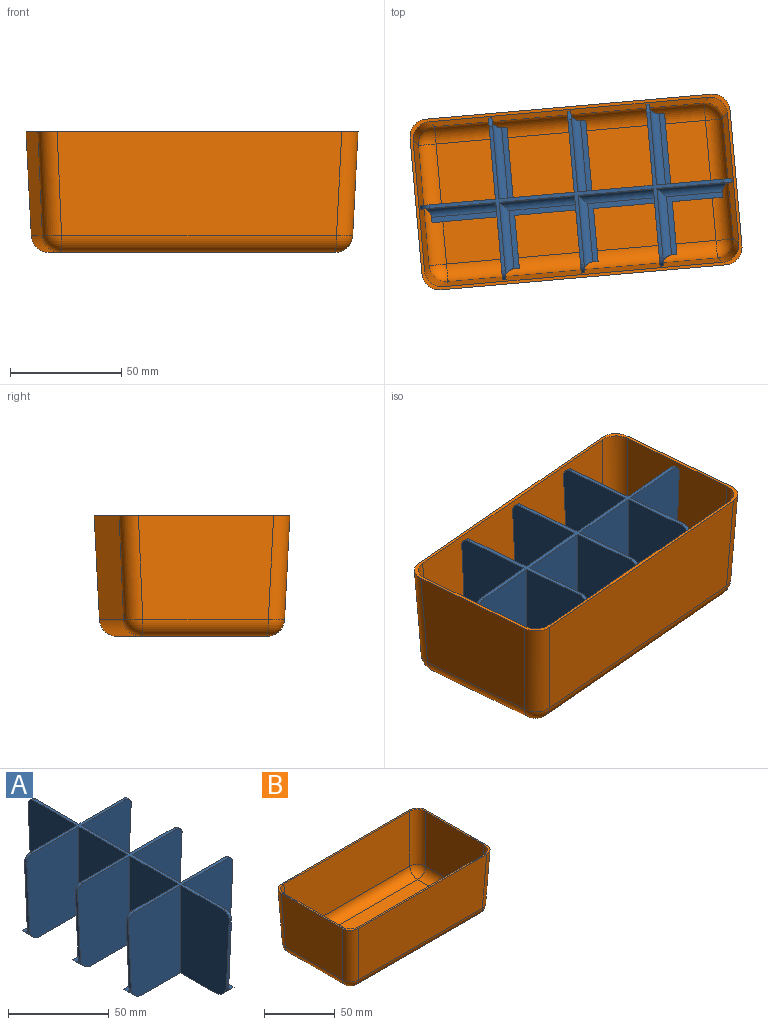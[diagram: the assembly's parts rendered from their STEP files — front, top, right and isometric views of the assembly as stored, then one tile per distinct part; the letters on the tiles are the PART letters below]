
ASSEMBLY  parts=2 mates=1
PART A: 73 faces, bbox 73.1x140.8x53 mm
  f0: plane 27.6x2mm, normal (1,0,0), area 55.2mm2, adj f8,f15,f36,f43
  f1: plane 29.36x2mm, normal (1,0,0), area 55.4mm2, adj f2,f15,f45,f54
  f2: plane 29.36x2.4mm, normal (0,0,1), area 70.5mm2, adj f1,f45,f54,f55
  f3: plane 47x34mm, normal (1,0,0), area 1598mm2, adj f17,f36,f44,f60
  f4: plane 47x34.01mm, normal (1,0,0), area 1551.4mm2, adj f17,f18,f45,f54,f55,f72
  f5: plane 53x34mm, normal (-1,0,0), area 1785.8mm2, adj f15,f17,f33,f39,f40,f41,f62
  f6: plane 53x34.01mm, normal (-1,0,0), area 1730.2mm2, adj f15,f17,f18,f42,f54,f72
  f7: plane 27.6x2mm, normal (1,0,0), area 55.2mm2, adj f12,f15,f27,f34
  f8: plane 30x26.31mm, normal (0,0,1), area 129.4mm2, adj f0,f36,f43,f48,f60,f61
  f9: plane 47x34mm, normal (1,0,0), area 1598mm2, adj f17,f27,f35,f58
  f10: plane 53x34mm, normal (-1,0,0), area 1785.8mm2, adj f15,f17,f24,f30,f31,f32,f63
  f11: plane 22.96x2mm, normal (1,0,0), area 42.6mm2, adj f15,f16,f25,f53
  f12: plane 30x26.31mm, normal (0,0,1), area 129.4mm2, adj f7,f27,f34,f50,f58,f59
  f13: plane 47x34.01mm, normal (1,0,0), area 1551.4mm2, adj f17,f19,f26,f53,f56,f71
  f14: plane 53x34.01mm, normal (-1,0,0), area 1714mm2, adj f15,f17,f19,f21,f22,f23,f53,f64
  f15: plane 120.94x53.24mm, normal (0,0,-1), area 2053.2mm2, adj f0,f1,f5,f6,f7,f10,f11,f14
  f16: plane 26.31x25.36mm, normal (0,0,1), area 118.3mm2, adj f11,f25,f52,f53,f56,f57
  f17: plane 132.81x65.11mm, normal (0,0,1), area 517.4mm2, adj f3,f4,f5,f6,f9,f10,f13,f14
  f18: plane 41.19x1.94mm, normal (0,-1,-0.05), area 66mm2, adj f4,f6,f54,f72
  f19: plane 41.19x1.94mm, normal (0,1,-0.05), area 66mm2, adj f13,f14,f53,f71
  f20: plane 41.19x1.94mm, normal (-1,0,-0.05), area 66mm2, adj f21,f24,f51,f69
  f21: plane 47x36.56mm, normal (0,1,0), area 1671.2mm2, adj f14,f17,f20,f51,f64,f69
  f22: plane 31.91x2.4mm, normal (0,0,1), area 76.6mm2, adj f14,f23,f51,f64
  f23: plane 31.91x2mm, normal (0,1,0), area 60.5mm2, adj f14,f15,f22,f51
  f24: plane 53x36.56mm, normal (0,-1,0), area 1865.4mm2, adj f10,f15,f17,f20,f51,f69
  f25: plane 23.91x2mm, normal (0,1,0), area 44.5mm2, adj f11,f15,f16,f52
  f26: plane 47x34.96mm, normal (0,1,0), area 1596mm2, adj f13,f17,f28,f52,f57,f70
  f27: plane 53x34.96mm, normal (0,-1,0), area 1764.4mm2, adj f7,f9,f12,f15,f17,f28,f52,f58
  f28: plane 41.19x1.94mm, normal (1,0,-0.05), area 66mm2, adj f26,f27,f52,f70
  f29: plane 41.19x1.94mm, normal (-1,0,-0.05), area 66mm2, adj f30,f33,f49,f67
  f30: plane 47x36.56mm, normal (0,1,0), area 1671.2mm2, adj f10,f17,f29,f49,f63,f67
  f31: plane 31.91x2.4mm, normal (0,0,1), area 76.6mm2, adj f10,f32,f49,f63
  f32: plane 31.91x2mm, normal (0,1,0), area 60.5mm2, adj f10,f15,f31,f49
  f33: plane 53x36.56mm, normal (0,-1,0), area 1865.4mm2, adj f5,f15,f17,f29,f49,f67
  f34: plane 23.91x2mm, normal (0,1,0), area 44.5mm2, adj f7,f12,f15,f50
  f35: plane 47x34.96mm, normal (0,1,0), area 1596mm2, adj f9,f17,f37,f50,f59,f68
  f36: plane 53x34.96mm, normal (0,-1,0), area 1764.4mm2, adj f0,f3,f8,f15,f17,f37,f50,f60
  f37: plane 41.19x1.94mm, normal (1,0,-0.05), area 66mm2, adj f35,f36,f50,f68
  f38: plane 41.19x1.94mm, normal (-1,0,-0.05), area 66mm2, adj f39,f42,f47,f65
  f39: plane 47x36.56mm, normal (0,1,0), area 1671.2mm2, adj f5,f17,f38,f47,f62,f65
  f40: plane 31.91x2.4mm, normal (0,0,1), area 76.6mm2, adj f5,f41,f47,f62
  f41: plane 31.91x2mm, normal (0,1,0), area 60.5mm2, adj f5,f15,f40,f47
  f42: plane 53x36.56mm, normal (0,-1,0), area 1865.4mm2, adj f6,f15,f17,f38,f47,f65
  f43: plane 23.91x2mm, normal (0,1,0), area 44.5mm2, adj f0,f8,f15,f48
  f44: plane 47x34.96mm, normal (0,1,0), area 1596mm2, adj f3,f17,f46,f48,f61,f66
  f45: plane 53x34.96mm, normal (0,-1,0), area 1764.4mm2, adj f1,f2,f4,f15,f17,f46,f48,f55
  f46: plane 41.19x1.94mm, normal (1,0,-0.05), area 66mm2, adj f44,f45,f48,f66
  f47: cylinder r=8mm len=8mm, axis (0,1,0), area 61.1mm2, adj f15,f38,f39,f40,f41,f42,f62
  f48: cylinder r=8mm len=8mm, axis (0,1,0), area 61.1mm2, adj f8,f15,f43,f44,f45,f46,f61
  f49: cylinder r=8mm len=8mm, axis (0,1,0), area 61.1mm2, adj f15,f29,f30,f31,f32,f33,f63
  f50: cylinder r=8mm len=8mm, axis (0,1,0), area 61.1mm2, adj f12,f15,f34,f35,f36,f37,f59
  f51: cylinder r=8mm len=8mm, axis (0,1,0), area 61.1mm2, adj f15,f20,f21,f22,f23,f24,f64
  f52: cylinder r=8mm len=8mm, axis (0,1,0), area 61.1mm2, adj f15,f16,f25,f26,f27,f28,f57
  f53: cylinder r=8mm len=8mm, axis (1,0,0), area 61.1mm2, adj f11,f13,f14,f15,f16,f19,f56
  f54: cylinder r=8mm len=8mm, axis (1,0,0), area 61.1mm2, adj f1,f2,f4,f6,f15,f18,f55
  f55: cylinder r=4mm len=31.82mm, axis (0,1,0), area 191.5mm2, adj f2,f4,f45,f54
  f56: cylinder r=4mm len=31.82mm, axis (0,1,0), area 182.4mm2, adj f13,f16,f53,f57
  f57: cylinder r=4mm len=32.77mm, axis (-1,0,0), area 188.4mm2, adj f16,f26,f52,f56
  f58: cylinder r=4mm len=34mm, axis (0,1,0), area 204.5mm2, adj f9,f12,f27,f59
  f59: cylinder r=4mm len=32.77mm, axis (-1,0,0), area 188.4mm2, adj f12,f35,f50,f58
  f60: cylinder r=4mm len=34mm, axis (0,1,0), area 204.5mm2, adj f3,f8,f36,f61
  f61: cylinder r=4mm len=32.77mm, axis (-1,0,0), area 188.4mm2, adj f8,f44,f48,f60
  f62: cylinder r=4mm len=34.37mm, axis (-1,0,0), area 207.6mm2, adj f5,f39,f40,f47
  f63: cylinder r=4mm len=34.37mm, axis (-1,0,0), area 207.6mm2, adj f10,f30,f31,f49
  f64: cylinder r=4mm len=34.37mm, axis (-1,0,0), area 207.6mm2, adj f14,f21,f22,f51
  f65: cylinder r=4mm len=4.19mm, axis (0,-1,0), area 10.4mm2, adj f17,f38,f39,f42
  f66: cylinder r=4mm len=4.19mm, axis (0,-1,0), area 10.4mm2, adj f17,f44,f45,f46
  f67: cylinder r=4mm len=4.19mm, axis (0,-1,0), area 10.4mm2, adj f17,f29,f30,f33
  f68: cylinder r=4mm len=4.19mm, axis (0,-1,0), area 10.4mm2, adj f17,f35,f36,f37
  f69: cylinder r=4mm len=4.19mm, axis (0,-1,0), area 10.4mm2, adj f17,f20,f21,f24
  f70: cylinder r=4mm len=4.19mm, axis (0,-1,0), area 10.4mm2, adj f17,f26,f27,f28
  f71: cylinder r=4mm len=4.19mm, axis (-1,0,0), area 10.4mm2, adj f13,f14,f17,f19
  f72: cylinder r=4mm len=4.19mm, axis (-1,0,0), area 10.4mm2, adj f4,f6,f17,f18
PART B: 35 faces, bbox 144.6x77.1x54.5 mm
  f0: plane 61.12x46.68mm, normal (1,0,-0.05), area 2753.1mm2, adj f8,f13,f16,f26
  f1: plane 128.62x46.68mm, normal (0,1,-0.05), area 5907.3mm2, adj f8,f13,f14,f22
  f2: plane 61.12x46.68mm, normal (-1,0,-0.05), area 2753.1mm2, adj f8,f14,f15,f19
  f3: plane 58.52x45.38mm, normal (1,0,0.05), area 2561.1mm2, adj f8,f9,f12,f32
  f4: plane 126.02x45.38mm, normal (0,-1,0.05), area 5627.4mm2, adj f8,f9,f10,f28
  f5: plane 58.52x45.38mm, normal (-1,0,0.05), area 2561.1mm2, adj f8,f10,f11,f29
  f6: plane 126.02x45.38mm, normal (0,1,0.05), area 5627.4mm2, adj f8,f11,f12,f33
  f7: plane 128.62x46.68mm, normal (0,-1,-0.05), area 5907.3mm2, adj f8,f15,f16,f23
  f8: plane 144.6x77.1mm, normal (0,0,1), area 569.7mm2, adj f0,f1,f2,f3,f4,f5,f6,f7
  f9: cylinder r=8mm len=45.69mm, axis (0.05,-0.05,-1), area 572mm2, adj f3,f4,f8,f30
  f10: cylinder r=8mm len=45.69mm, axis (-0.05,-0.05,-1), area 572mm2, adj f4,f5,f8,f27
  f11: cylinder r=8mm len=45.69mm, axis (-0.05,0.05,-1), area 572mm2, adj f5,f6,f8,f31
  f12: cylinder r=8mm len=45.69mm, axis (0.05,0.05,-1), area 572mm2, adj f3,f6,f8,f34
  f13: cylinder r=8mm len=46.99mm, axis (0.05,0.05,1), area 588.3mm2, adj f0,f1,f8,f24
  f14: cylinder r=8mm len=46.99mm, axis (-0.05,0.05,1), area 588.3mm2, adj f1,f2,f8,f20
  f15: cylinder r=8mm len=46.99mm, axis (-0.05,-0.05,1), area 588.3mm2, adj f2,f7,f8,f21
  f16: cylinder r=8mm len=46.99mm, axis (0.05,-0.05,1), area 588.3mm2, adj f0,f7,f8,f25
  f17: plane 121.74x54.24mm, normal (0,0,1), area 6602.8mm2, adj f28,f29,f32,f33
  f18: plane 124.22x56.72mm, normal (0,0,-1), area 7044.9mm2, adj f19,f22,f23,f26
  f19: cylinder r=8mm len=56.72mm, axis (0,1,0), area 691.3mm2, adj f2,f18,f20,f21
  f20: sphere r=8mm, area 94.5mm2, adj f14,f19,f22
  f21: sphere r=8mm, area 94.5mm2, adj f15,f19,f23
  f22: cylinder r=8mm len=124.22mm, axis (1,0,0), area 1514.1mm2, adj f1,f18,f20,f24
  f23: cylinder r=8mm len=124.22mm, axis (1,0,0), area 1514.1mm2, adj f7,f18,f21,f25
  f24: sphere r=8mm, area 94.5mm2, adj f13,f22,f26
  f25: sphere r=8mm, area 94.5mm2, adj f16,f23,f26
  f26: cylinder r=8mm len=56.72mm, axis (0,-1,0), area 691.3mm2, adj f0,f18,f24,f25
  f27: sphere r=8mm, area 94.5mm2, adj f10,f28,f29
  f28: cylinder r=8mm len=121.74mm, axis (-1,0,0), area 1483.9mm2, adj f4,f17,f27,f30
  f29: cylinder r=8mm len=54.24mm, axis (0,-1,0), area 661.1mm2, adj f5,f17,f27,f31
  f30: sphere r=8mm, area 94.5mm2, adj f9,f28,f32
  f31: sphere r=8mm, area 94.5mm2, adj f11,f29,f33
  f32: cylinder r=8mm len=54.24mm, axis (0,-1,0), area 661.1mm2, adj f3,f17,f30,f34
  f33: cylinder r=8mm len=121.74mm, axis (-1,0,0), area 1483.9mm2, adj f6,f17,f31,f34
  f34: sphere r=8mm, area 94.5mm2, adj f12,f32,f33
PLACE A rot(axis=(0,0,-1),85deg) t=(-0.85,4.73,-15.91)mm
PLACE B rot(axis=(0,0,1),5deg) t=(-0.85,4.73,-15.91)mm
MATE revolute A.f15 <-> B.f17  axis (0,0,1) through (-0.85,4.73,-15.91)mm
